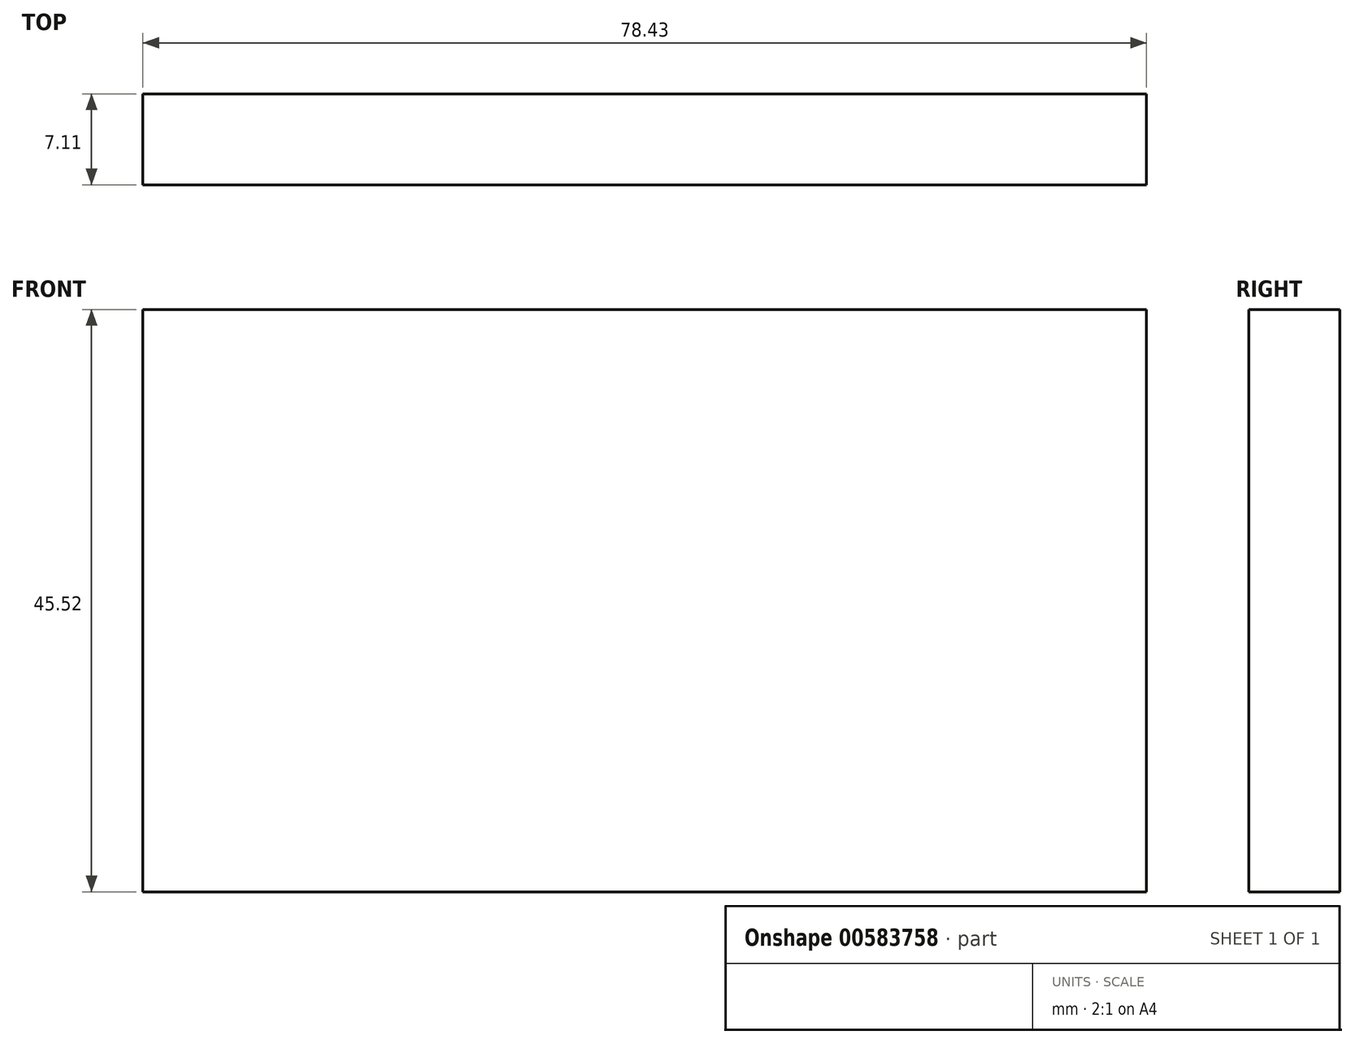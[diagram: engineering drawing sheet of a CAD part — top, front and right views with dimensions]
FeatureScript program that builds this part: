
annotation { "Feature Type Name" : "Feature", "Feature Type Description" : "" }
export const myFeature = defineFeature(function(context is Context, id is Id, definition is map)
    precondition{}
    {
        {
            var Q0;
            Q0=qCreatedBy(makeId("Front.planeOp"),FACE);
            var sketch = newSketch(context, id + "F0", { "sketchPlane" : qUnion([Q0])});
            skLineSegment(sketch, "E0.bottom", {"start": v(-38.92, 22.76) * mm, "end": v(39.51, 22.76) * mm});
            skLineSegment(sketch, "E0.top", {"start": v(-38.92, -22.76) * mm, "end": v(39.51, -22.76) * mm});
            skLineSegment(sketch, "E0.left", {"start": v(-38.92, 22.76) * mm, "end": v(-38.92, -22.76) * mm});
            skLineSegment(sketch, "E0.right", {"start": v(39.51, 22.76) * mm, "end": v(39.51, -22.76) * mm});
            skSolve(sketch);
        }
        {
            var Q0;
            Q0 = qSketchRegion(id + "F0", true);
            extrude(context, id + "F1", {"entities" : qUnion([Q0]), "depth" : 7.11 * mm, "offsetDistance" : 25.4 * mm});
        }
    });
